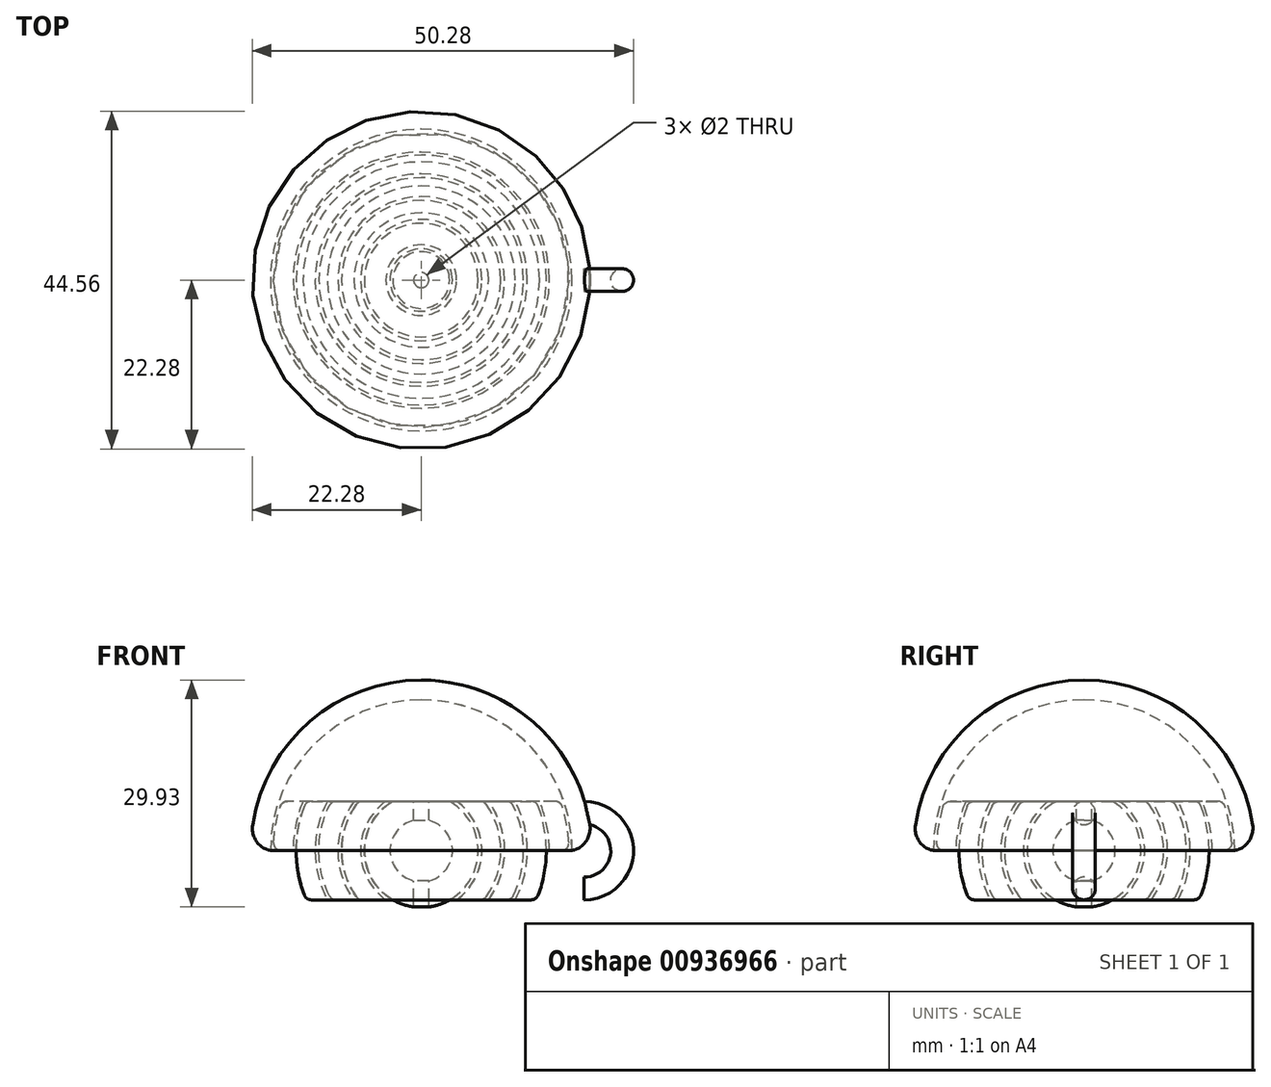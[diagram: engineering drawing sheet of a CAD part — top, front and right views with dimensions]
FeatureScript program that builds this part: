
annotation { "Feature Type Name" : "Feature", "Feature Type Description" : "" }
export const myFeature = defineFeature(function(context is Context, id is Id, definition is map)
    precondition{}
    {
        {
            var Q0;
            Q0=qCreatedBy(makeId("Front.planeOp"),FACE);
            var sketch = newSketch(context, id + "F0", { "sketchPlane" : qUnion([Q0])});
            skCircle(sketch, "E0", {"center": v(0, 0) * mm, "radius": 22.5 * mm});
            skCircle(sketch, "E1", {"center": v(0, 0) * mm, "radius": 19.9 * mm});
            skCircle(sketch, "E2", {"center": v(0, 0) * mm, "radius": 19.5 * mm});
            skCircle(sketch, "E3", {"center": v(0, 0) * mm, "radius": 16.9 * mm});
            skCircle(sketch, "E4", {"center": v(0, 0) * mm, "radius": 16.5 * mm});
            skCircle(sketch, "E5", {"center": v(0, 0) * mm, "radius": 14 * mm});
            skCircle(sketch, "E6", {"center": v(0, 0) * mm, "radius": 13.5 * mm});
            skCircle(sketch, "E7", {"center": v(0, 0) * mm, "radius": 11 * mm});
            skCircle(sketch, "E8", {"center": v(0, 0) * mm, "radius": 10.5 * mm});
            skCircle(sketch, "E9", {"center": v(0, 0) * mm, "radius": 8 * mm});
            skCircle(sketch, "E10", {"center": v(0, 0) * mm, "radius": 7.5 * mm});
            skCircle(sketch, "E11", {"center": v(0, 0) * mm, "radius": 4.11 * mm});
            skLineSegment(sketch, "E12", {"start": v(0, 24.67) * mm, "end": v(0, -27.98) * mm});
            skLineSegment(sketch, "E13", {"start": v(-21.54, 6.5) * mm, "end": v(21.54, 6.5) * mm});
            skLineSegment(sketch, "E14", {"start": v(-22.5, 0) * mm, "end": v(22.5, 0) * mm});
            skLineSegment(sketch, "E15.trimOffspring", {"start": v(-21.54, -6.5) * mm, "end": v(21.54, -6.5) * mm});
            skSolve(sketch);
        }
        {
            var Q0;
            {var subQ0=sQuery(id+"F0.wireOp",EDGE,"E13");var subQ1=sQuery(id+"F0.wireOp",EDGE,"E10");var subQ2=makeQuery(id+"F0.imprint","INTERSECT",VERTEX,{"disambiguationData":[OD(1.0)],"derivedFrom":[subQ1,subQ0]});Q0=makeQuery(id+"F0.imprint","IMPRINT",FACE,{"disambiguationData":[TD([[makeQuery(id+"F0.imprint","IMPRINT",EDGE,{"disambiguationData":[TD([[subQ2,-1.0]])],"derivedFrom":subQ1}),1.0]])]});}
            var Q1;
            {var subQ0=sQuery(id+"F0.wireOp",EDGE,"E14");var subQ1=sQuery(id+"F0.wireOp",EDGE,"E10");var subQ2=makeQuery(id+"F0.imprint","INTERSECT",VERTEX,{"disambiguationData":[OD(1.0)],"derivedFrom":[subQ1,subQ0]});Q1=makeQuery(id+"F0.imprint","IMPRINT",FACE,{"disambiguationData":[TD([[makeQuery(id+"F0.imprint","IMPRINT",EDGE,{"disambiguationData":[TD([[subQ2,-1.0]])],"derivedFrom":subQ1}),1.0]])]});}
            var Q2;
            {var subQ0=sQuery(id+"F0.wireOp",EDGE,"E12");var subQ1=sQuery(id+"F0.wireOp",EDGE,"E10");var subQ2=makeQuery(id+"F0.imprint","INTERSECT",VERTEX,{"disambiguationData":[OD(0.0)],"derivedFrom":[subQ1,subQ0]});Q2=makeQuery(id+"F0.imprint","IMPRINT",FACE,{"disambiguationData":[TD([[makeQuery(id+"F0.imprint","IMPRINT",EDGE,{"disambiguationData":[TD([[subQ2,-1.0]])],"derivedFrom":subQ1}),1.0]])]});}
            var Q3;
            Q3=sQuery(id+"F0.wireOp",EDGE,"E12");
            revolve(context, id + "F1", {"surfaceOperationType" : NewSurfaceOperationType.NEW, "entities" : qUnion([Q0, Q1, Q2]), "axis" : qUnion([Q3]), "revolveType" : RevolveType.FULL});
        }
        {
            var Q0;
            {var subQ0=sQuery(id+"F0.wireOp",EDGE,"E13");var subQ1=sQuery(id+"F0.wireOp",EDGE,"E8");var subQ2=makeQuery(id+"F0.imprint","INTERSECT",VERTEX,{"disambiguationData":[OD(1.0)],"derivedFrom":[subQ1,subQ0]});Q0=makeQuery(id+"F0.imprint","IMPRINT",FACE,{"disambiguationData":[TD([[makeQuery(id+"F0.imprint","IMPRINT",EDGE,{"disambiguationData":[TD([[subQ2,-1.0]])],"derivedFrom":subQ1}),1.0]])]});}
            var Q1;
            {var subQ0=sQuery(id+"F0.wireOp",EDGE,"E14");var subQ1=sQuery(id+"F0.wireOp",EDGE,"E8");var subQ2=makeQuery(id+"F0.imprint","INTERSECT",VERTEX,{"disambiguationData":[OD(1.0)],"derivedFrom":[subQ1,subQ0]});Q1=makeQuery(id+"F0.imprint","IMPRINT",FACE,{"disambiguationData":[TD([[makeQuery(id+"F0.imprint","IMPRINT",EDGE,{"disambiguationData":[TD([[subQ2,-1.0]])],"derivedFrom":subQ1}),1.0]])]});}
            var Q2;
            Q2=sQuery(id+"F0.wireOp",EDGE,"E12");
            revolve(context, id + "F2", {"surfaceOperationType" : NewSurfaceOperationType.NEW, "entities" : qUnion([Q0, Q1]), "axis" : qUnion([Q2]), "revolveType" : RevolveType.FULL});
        }
        {
            var Q0;
            {var subQ0=sQuery(id+"F0.wireOp",EDGE,"E13");var subQ1=sQuery(id+"F0.wireOp",EDGE,"E6");var subQ2=makeQuery(id+"F0.imprint","INTERSECT",VERTEX,{"disambiguationData":[OD(1.0)],"derivedFrom":[subQ1,subQ0]});Q0=makeQuery(id+"F0.imprint","IMPRINT",FACE,{"disambiguationData":[TD([[makeQuery(id+"F0.imprint","IMPRINT",EDGE,{"disambiguationData":[TD([[subQ2,-1.0]])],"derivedFrom":subQ1}),1.0]])]});}
            var Q1;
            {var subQ0=sQuery(id+"F0.wireOp",EDGE,"E14");var subQ1=sQuery(id+"F0.wireOp",EDGE,"E6");var subQ2=makeQuery(id+"F0.imprint","INTERSECT",VERTEX,{"disambiguationData":[OD(1.0)],"derivedFrom":[subQ1,subQ0]});Q1=makeQuery(id+"F0.imprint","IMPRINT",FACE,{"disambiguationData":[TD([[makeQuery(id+"F0.imprint","IMPRINT",EDGE,{"disambiguationData":[TD([[subQ2,-1.0]])],"derivedFrom":subQ1}),1.0]])]});}
            var Q2;
            Q2=sQuery(id+"F0.wireOp",EDGE,"E12");
            revolve(context, id + "F3", {"surfaceOperationType" : NewSurfaceOperationType.NEW, "entities" : qUnion([Q0, Q1]), "axis" : qUnion([Q2]), "revolveType" : RevolveType.FULL});
        }
        {
            var Q0;
            {var subQ0=sQuery(id+"F0.wireOp",EDGE,"E13");var subQ1=sQuery(id+"F0.wireOp",EDGE,"E4");var subQ2=makeQuery(id+"F0.imprint","INTERSECT",VERTEX,{"disambiguationData":[OD(1.0)],"derivedFrom":[subQ1,subQ0]});Q0=makeQuery(id+"F0.imprint","IMPRINT",FACE,{"disambiguationData":[TD([[makeQuery(id+"F0.imprint","IMPRINT",EDGE,{"disambiguationData":[TD([[subQ2,-1.0]])],"derivedFrom":subQ1}),1.0]])]});}
            var Q1;
            {var subQ0=sQuery(id+"F0.wireOp",EDGE,"E14");var subQ1=sQuery(id+"F0.wireOp",EDGE,"E4");var subQ2=makeQuery(id+"F0.imprint","INTERSECT",VERTEX,{"disambiguationData":[OD(1.0)],"derivedFrom":[subQ1,subQ0]});Q1=makeQuery(id+"F0.imprint","IMPRINT",FACE,{"disambiguationData":[TD([[makeQuery(id+"F0.imprint","IMPRINT",EDGE,{"disambiguationData":[TD([[subQ2,-1.0]])],"derivedFrom":subQ1}),1.0]])]});}
            var Q2;
            Q2=sQuery(id+"F0.wireOp",EDGE,"E12");
            revolve(context, id + "F4", {"surfaceOperationType" : NewSurfaceOperationType.NEW, "entities" : qUnion([Q0, Q1]), "axis" : qUnion([Q2]), "revolveType" : RevolveType.FULL});
        }
        {
            var Q0;
            {var subQ0=sQuery(id+"F0.wireOp",EDGE,"E13");var subQ1=sQuery(id+"F0.wireOp",EDGE,"E2");var subQ2=makeQuery(id+"F0.imprint","INTERSECT",VERTEX,{"disambiguationData":[OD(1.0)],"derivedFrom":[subQ1,subQ0]});Q0=makeQuery(id+"F0.imprint","IMPRINT",FACE,{"disambiguationData":[TD([[makeQuery(id+"F0.imprint","IMPRINT",EDGE,{"disambiguationData":[TD([[subQ2,-1.0]])],"derivedFrom":subQ1}),1.0]])]});}
            var Q1;
            {var subQ0=sQuery(id+"F0.wireOp",EDGE,"E14");var subQ1=sQuery(id+"F0.wireOp",EDGE,"E2");var subQ2=makeQuery(id+"F0.imprint","INTERSECT",VERTEX,{"disambiguationData":[OD(1.0)],"derivedFrom":[subQ1,subQ0]});Q1=makeQuery(id+"F0.imprint","IMPRINT",FACE,{"disambiguationData":[TD([[makeQuery(id+"F0.imprint","IMPRINT",EDGE,{"disambiguationData":[TD([[subQ2,-1.0]])],"derivedFrom":subQ1}),1.0]])]});}
            var Q2;
            Q2=sQuery(id+"F0.wireOp",EDGE,"E12");
            revolve(context, id + "F5", {"surfaceOperationType" : NewSurfaceOperationType.NEW, "entities" : qUnion([Q0, Q1]), "axis" : qUnion([Q2]), "revolveType" : RevolveType.FULL});
        }
        {
            var Q0;
            {var subQ0=sQuery(id+"F0.wireOp",EDGE,"E13");var subQ1=sQuery(id+"F0.wireOp",EDGE,"E0");var subQ2=makeQuery(id+"F0.imprint","INTERSECT",VERTEX,{"disambiguationData":[OD(0.0)],"derivedFrom":[subQ1,subQ0]});Q0=makeQuery(id+"F0.imprint","IMPRINT",FACE,{"disambiguationData":[TD([[makeQuery(id+"F0.imprint","IMPRINT",EDGE,{"disambiguationData":[TD([[subQ2,-1.0]])],"derivedFrom":subQ1}),1.0]])]});}
            var Q1;
            {var subQ0=sQuery(id+"F0.wireOp",EDGE,"E14");var subQ1=sQuery(id+"F0.wireOp",EDGE,"E0");var subQ2=makeQuery(id+"F0.imprint","INTERSECT",VERTEX,{"disambiguationData":[OD(0.0)],"derivedFrom":[subQ1,subQ0]});Q1=makeQuery(id+"F0.imprint","IMPRINT",FACE,{"disambiguationData":[TD([[makeQuery(id+"F0.imprint","IMPRINT",EDGE,{"disambiguationData":[TD([[subQ2,-1.0]])],"derivedFrom":subQ1}),1.0]])]});}
            var Q2;
            Q2=sQuery(id+"F0.wireOp",EDGE,"E12");
            revolve(context, id + "F6", {"surfaceOperationType" : NewSurfaceOperationType.NEW, "entities" : qUnion([Q0, Q1]), "axis" : qUnion([Q2]), "revolveType" : RevolveType.FULL});
        }
        {
            var Q0;
            Q0=qCreatedBy(makeId("Right.planeOp"),FACE);
            var Q1;
            Q1 = qBodyType(qCreatedBy(id + "F8" ,EDGE), BodyType.WIRE);
            cPlane(context, id + "F7", {"entities" : qUnion([Q0, Q1]), "cplaneType" : CPlaneType.OFFSET, "offset" : 21.5 * mm, "width" : 150 * mm, "height" : 150 * mm});
        }
        {
            var Q0;
            Q0=qCreatedBy(id+"F7.planeOp",FACE);
            var sketch = newSketch(context, id + "F8", { "sketchPlane" : qUnion([Q0])});
            skCircle(sketch, "E16", {"center": v(0, 5) * mm, "radius": 1.5 * mm});
            skPoint(sketch, "E16.first.point", {"position": v(0, 6.5) * mm});
            skPoint(sketch, "E16.second.point", {"position": v(0, 3.5) * mm});
            skPoint(sketch, "E16.third.point", {"position": v(1.27, 4.2) * mm});
            skLineSegment(sketch, "E17", {"start": v(-33.93, 0) * mm, "end": v(45.1, 0) * mm});
            skSolve(sketch);
        }
        {
            var Q0;
            Q0 = qSketchRegion(id + "F8", true);
            var Q1;
            Q1=sQuery(id+"F8.wireOp",EDGE,"E17");
            revolve(context, id + "F9", {"operationType" : NewBodyOperationType.ADD, "surfaceOperationType" : NewSurfaceOperationType.NEW, "entities" : qUnion([Q0]), "axis" : qUnion([Q1]), "revolveType" : RevolveType.ONE_DIRECTION, "angle" : 180 * degree});
        }
        {
            var Q0;
            Q0=qCreatedBy(makeId("Top.planeOp"),FACE);
            var Q1;
            Q1=qCreatedBy(makeId("Top.planeOp"),FACE);
            var sketch = newSketch(context, id + "F10", { "sketchPlane" : qUnion([Q0, Q1])});
            skCircle(sketch, "E18", {"center": v(0, 0) * mm, "radius": 1 * mm});
            skSolve(sketch);
        }
        {
            var Q0;
            Q0 = qSketchRegion(id + "F10", true);
            extrude(context, id + "F11", {"entities" : qUnion([Q0]), "operationType" : NewBodyOperationType.REMOVE, "endBound" : BoundingType.SYMMETRIC, "oppositeDirection" : true, "depth" : 25 * mm, "offsetDistance" : 25 * mm});
        }
        {
            var Q0;
            Q0=makeQuery(id+"F6.opRevolve","SWEPT_EDGE",EDGE,{"disambiguationData":[OSD([sQuery(id+"F0.wireOp",EDGE,"E0"),sQuery(id+"F0.wireOp",EDGE,"E13")])]});
            var Q1;
            Q1=makeQuery(id+"F6.opRevolve","SWEPT_EDGE",EDGE,{"disambiguationData":[OSD([sQuery(id+"F0.wireOp",EDGE,"E0"),sQuery(id+"F0.wireOp",EDGE,"E15.trimOffspring")])]});
            fillet(context, id + "F12", {"entities" : qUnion([Q0, Q1]), "radius" : 3 * mm, "tangentPropagation" : true, "allowEdgeOverflow" : false});
        }
        {
            var Q0;
            Q0=makeQuery(id+"F5.opRevolve","SWEPT_EDGE",EDGE,{"disambiguationData":[OSD([sQuery(id+"F0.wireOp",EDGE,"E2"),sQuery(id+"F0.wireOp",EDGE,"E13")])]});
            fillet(context, id + "F13", {"entities" : qUnion([Q0]), "radius" : 1 * mm, "tangentPropagation" : true, "allowEdgeOverflow" : false});
        }
        {
            var Q0;
            Q0=makeQuery(id+"F4.opRevolve","SWEPT_EDGE",EDGE,{"disambiguationData":[OSD([sQuery(id+"F0.wireOp",EDGE,"E4"),sQuery(id+"F0.wireOp",EDGE,"E13")])]});
            var Q1;
            Q1=makeQuery(id+"F3.opRevolve","SWEPT_EDGE",EDGE,{"disambiguationData":[OSD([sQuery(id+"F0.wireOp",EDGE,"E6"),sQuery(id+"F0.wireOp",EDGE,"E13")])]});
            var Q2;
            Q2=makeQuery(id+"F2.opRevolve","SWEPT_EDGE",EDGE,{"disambiguationData":[OSD([sQuery(id+"F0.wireOp",EDGE,"E8"),sQuery(id+"F0.wireOp",EDGE,"E13")])]});
            var Q3;
            Q3=makeQuery(id+"F1.opRevolve","SWEPT_EDGE",EDGE,{"disambiguationData":[OSD([sQuery(id+"F0.wireOp",EDGE,"E10"),sQuery(id+"F0.wireOp",EDGE,"E13")])]});
            var Q4;
            Q4=makeQuery(id+"F5.opRevolve","SWEPT_EDGE",EDGE,{"disambiguationData":[OSD([sQuery(id+"F0.wireOp",EDGE,"E2"),sQuery(id+"F0.wireOp",EDGE,"E15.trimOffspring")])]});
            var Q5;
            Q5=makeQuery(id+"F4.opRevolve","SWEPT_EDGE",EDGE,{"disambiguationData":[OSD([sQuery(id+"F0.wireOp",EDGE,"E4"),sQuery(id+"F0.wireOp",EDGE,"E15.trimOffspring")])]});
            var Q6;
            Q6=makeQuery(id+"F3.opRevolve","SWEPT_EDGE",EDGE,{"disambiguationData":[OSD([sQuery(id+"F0.wireOp",EDGE,"E6"),sQuery(id+"F0.wireOp",EDGE,"E15.trimOffspring")])]});
            var Q7;
            Q7=makeQuery(id+"F2.opRevolve","SWEPT_EDGE",EDGE,{"disambiguationData":[OSD([sQuery(id+"F0.wireOp",EDGE,"E8"),sQuery(id+"F0.wireOp",EDGE,"E15.trimOffspring")])]});
            var Q8;
            Q8=makeQuery(id+"F1.opRevolve","SWEPT_EDGE",EDGE,{"disambiguationData":[OSD([sQuery(id+"F0.wireOp",EDGE,"E10"),sQuery(id+"F0.wireOp",EDGE,"E15.trimOffspring")])]});
            fillet(context, id + "F14", {"entities" : qUnion([Q0, Q1, Q2, Q3, Q4, Q5, Q6, Q7, Q8]), "radius" : 1 * mm, "tangentPropagation" : true, "allowEdgeOverflow" : false});
        }
        {
            var Q0;
            Q0=makeQuery(id+"F3.opRevolve","SWEPT_FACE",FACE,{"disambiguationData":[OSD([sQuery(id+"F0.wireOp",EDGE,"E13")])]});
            var Q1;
            Q1=makeQuery(id+"F2.opRevolve","SWEPT_FACE",FACE,{"disambiguationData":[OSD([sQuery(id+"F0.wireOp",EDGE,"E13")])]});
            var Q2;
            Q2=makeQuery(id+"F2.opRevolve","SWEPT_FACE",FACE,{"disambiguationData":[OSD([sQuery(id+"F0.wireOp",EDGE,"E13")])]});
            var Q3;
            Q3=makeQuery(id+"F3.opRevolve","SWEPT_FACE",FACE,{"disambiguationData":[OSD([sQuery(id+"F0.wireOp",EDGE,"E13")])]});
            var Q4;
            Q4=makeQuery(id+"F2.opRevolve","SWEPT_FACE",FACE,{"disambiguationData":[OSD([sQuery(id+"F0.wireOp",EDGE,"E13")])]});
            cPlane(context, id + "F15", {"entities" : qUnion([Q0, Q1, Q2, Q3, Q4]), "cplaneType" : CPlaneType.MID_PLANE, "offset" : 25 * mm, "width" : 150 * mm, "height" : 150 * mm});
        }
    });
